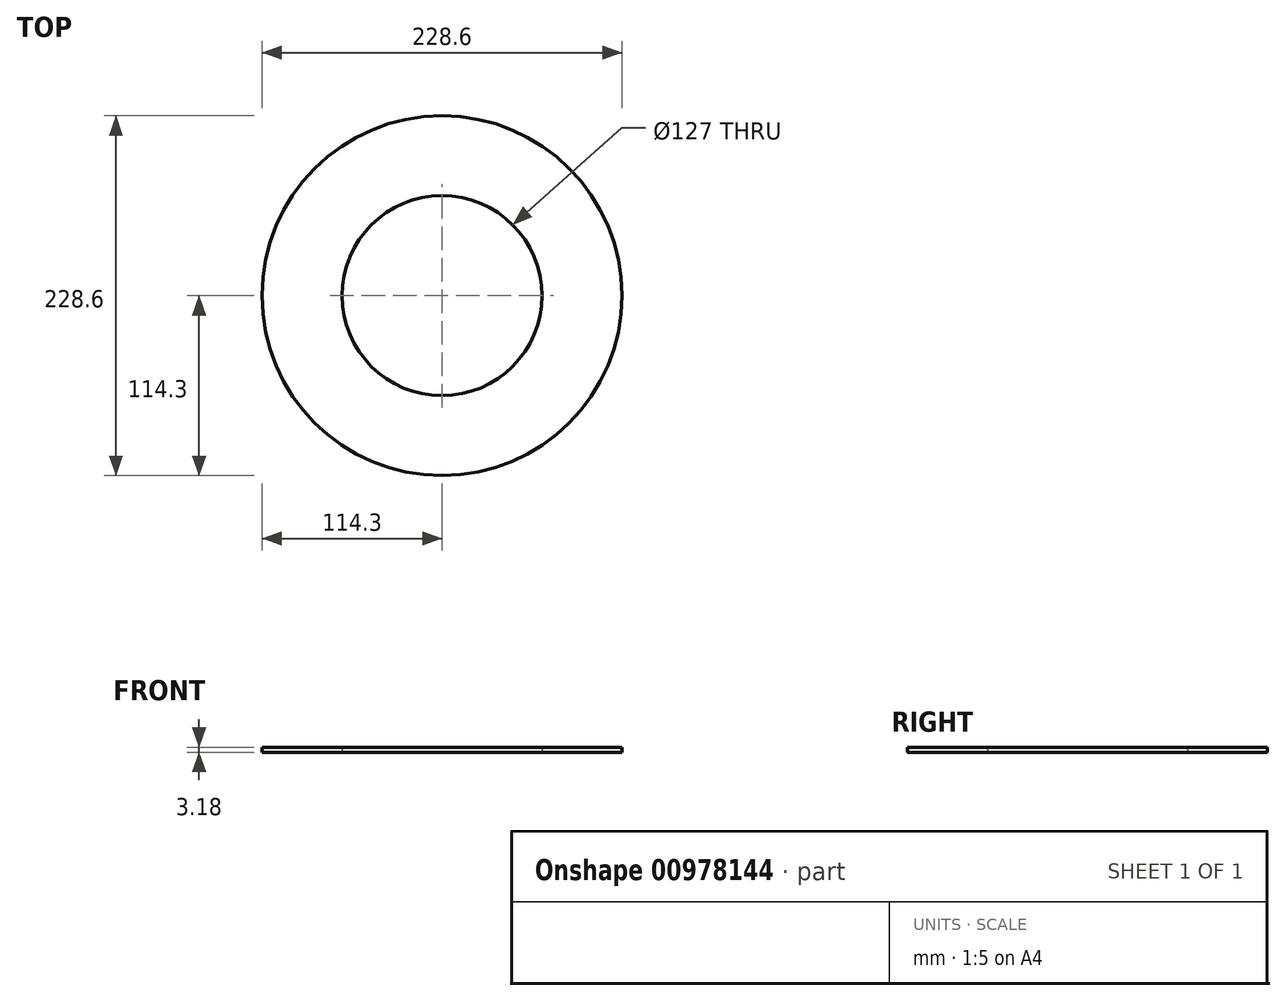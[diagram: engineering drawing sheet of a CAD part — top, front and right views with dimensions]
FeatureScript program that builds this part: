
annotation { "Feature Type Name" : "Feature", "Feature Type Description" : "" }
export const myFeature = defineFeature(function(context is Context, id is Id, definition is map)
    precondition{}
    {
        {
            var Q0;
            Q0=qCreatedBy(makeId("Top.planeOp"),FACE);
            var sketch = newSketch(context, id + "F0", { "sketchPlane" : qUnion([Q0])});
            skCircle(sketch, "E0", {"center": v(0, 0) * mm, "radius": 114.3 * mm});
            skPoint(sketch, "E1.right.end.orphan", {"position": v(-89.4, 12.7) * mm});
            skPoint(sketch, "E1.right.start.orphan", {"position": v(-89.4, -12.7) * mm});
            skPoint(sketch, "E1.left.end.orphan", {"position": v(89.4, 12.7) * mm});
            skPoint(sketch, "E1.left.start.orphan", {"position": v(89.4, -12.7) * mm});
            skCircle(sketch, "E2", {"center": v(0, 0) * mm, "radius": 63.5 * mm});
            skSolve(sketch);
        }
        {
            var Q0;
            Q0=makeQuery(id+"F0.imprint","IMPRINT",FACE,{"disambiguationData":[TD([[makeQuery(id+"F0.imprint","IMPRINT",EDGE,{"derivedFrom":sQuery(id+"F0.wireOp",EDGE,"E0")}),1.0]])]});
            extrude(context, id + "F1", {"entities" : qUnion([Q0]), "depth" : 3.17 * mm, "offsetDistance" : 25.4 * mm});
        }
    });
